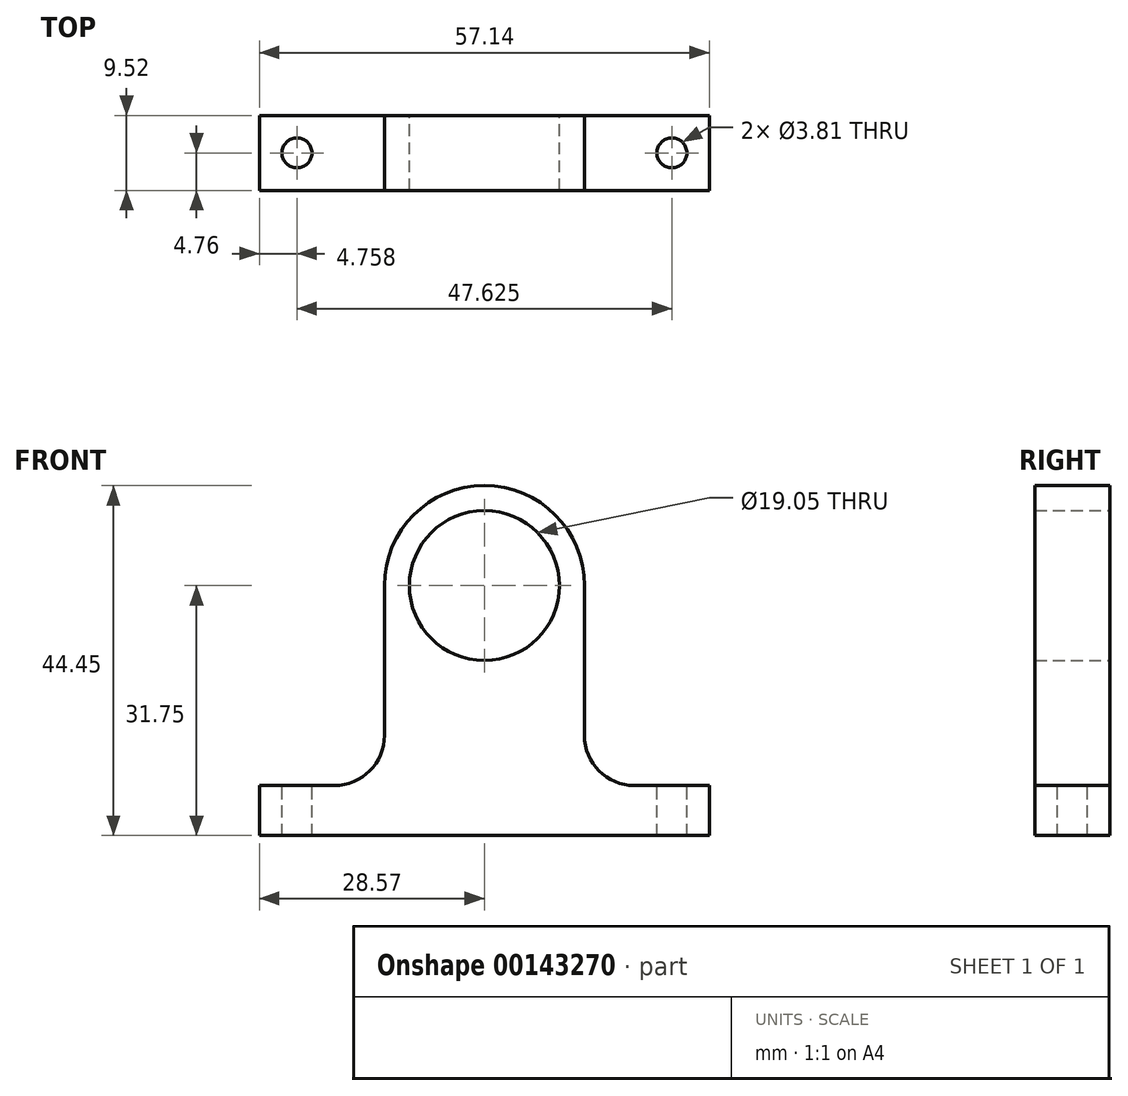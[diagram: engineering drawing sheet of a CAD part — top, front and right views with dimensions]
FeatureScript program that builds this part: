
annotation { "Feature Type Name" : "Feature", "Feature Type Description" : "" }
export const myFeature = defineFeature(function(context is Context, id is Id, definition is map)
    precondition{}
    {
        {
            var Q0;
            Q0=qCreatedBy(makeId("Front.planeOp"),FACE);
            var sketch = newSketch(context, id + "F0", { "sketchPlane" : qUnion([Q0])});
            skCircle(sketch, "E0", {"center": v(0, 0) * mm, "radius": 9.53 * mm});
            skArc(sketch, "E1", {"start": v(12.7, 0) * mm, "mid": v(0, 12.7) * mm, "end": v(-12.7, 0) * mm});
            skLineSegment(sketch, "E2", {"start": v(-12.7, 0) * mm, "end": v(-12.7, -25.4) * mm});
            skLineSegment(sketch, "E3", {"start": v(-12.7, -25.4) * mm, "end": v(-28.57, -25.4) * mm});
            skLineSegment(sketch, "E4", {"start": v(-28.58, -25.4) * mm, "end": v(-28.58, -31.75) * mm});
            skLineSegment(sketch, "E5", {"start": v(-28.58, -31.75) * mm, "end": v(28.57, -31.75) * mm});
            skLineSegment(sketch, "E6", {"start": v(28.57, -31.75) * mm, "end": v(28.57, -25.4) * mm});
            skLineSegment(sketch, "E7", {"start": v(28.57, -25.4) * mm, "end": v(12.7, -25.4) * mm});
            skLineSegment(sketch, "E8", {"start": v(12.7, -25.4) * mm, "end": v(12.7, 0) * mm});
            skCircle(sketch, "E9", {"center": v(0, 0) * mm, "radius": 4.76 * mm});
            skCircle(sketch, "E10", {"center": v(-4.76, 0) * mm, "radius": 4.76 * mm});
            skSolve(sketch);
        }
        {
            var Q0;
            Q0=makeQuery(id+"F0.imprint","IMPRINT",FACE,{"disambiguationData":[TD([[makeQuery(id+"F0.imprint","IMPRINT",EDGE,{"derivedFrom":sQuery(id+"F0.wireOp",EDGE,"E0")}),-1.0]])]});
            extrude(context, id + "F1", {"entities" : qUnion([Q0]), "depth" : 9.52 * mm, "symmetric" : true});
        }
        {
            var Q0;
            Q0=makeQuery(id+"F1.opExtrude","SWEPT_EDGE",EDGE,{"disambiguationData":[OSD([sQuery(id+"F0.wireOp",EDGE,"E2"),sQuery(id+"F0.wireOp",EDGE,"E3")])]});
            var Q1;
            Q1=makeQuery(id+"F1.opExtrude","SWEPT_EDGE",EDGE,{"disambiguationData":[OSD([sQuery(id+"F0.wireOp",EDGE,"E7"),sQuery(id+"F0.wireOp",EDGE,"E8")])]});
            fillet(context, id + "F2", {"entities" : qUnion([Q0, Q1]), "radius" : 6.35 * mm, "tangentPropagation" : true, "allowEdgeOverflow" : false});
        }
        {
            var Q0;
            Q0=makeQuery(id+"F1.opExtrude","SWEPT_FACE",FACE,{"disambiguationData":[OSD([sQuery(id+"F0.wireOp",EDGE,"E5")])]});
            var sketch = newSketch(context, id + "F3", { "sketchPlane" : qUnion([Q0])});
            skCircle(sketch, "E11", {"center": v(-23.81, 0) * mm, "radius": 1.87 * mm});
            skCircle(sketch, "E12", {"center": v(23.81, 0) * mm, "radius": 1.83 * mm});
            skSolve(sketch);
        }
        {
            var Q0;
            Q0=sQuery(id+"F3.wireOp",VERTEX,"E11.center");
            var Q1;
            Q1=sQuery(id+"F3.wireOp",VERTEX,"E12.center");
            var Q2;
            Q2=makeQuery(id+"F1.opExtrude","SWEPT_BODY",BODY,{"disambiguationData":[OSD([sQuery(id+"F0.wireOp",EDGE,"E0"),sQuery(id+"F0.wireOp",EDGE,"E1"),sQuery(id+"F0.wireOp",EDGE,"E2"),sQuery(id+"F0.wireOp",EDGE,"E3"),sQuery(id+"F0.wireOp",EDGE,"E4"),sQuery(id+"F0.wireOp",EDGE,"E5"),sQuery(id+"F0.wireOp",EDGE,"E6"),sQuery(id+"F0.wireOp",EDGE,"E7"),sQuery(id+"F0.wireOp",EDGE,"E8")])]});
            hole(context, id + "F4", {"style" : HoleStyle.SIMPLE, "endStyle" : HoleEndStyle.THROUGH, "holeDiameter" : 3.8 * mm, "locations" : qUnion([Q0, Q1]), "scope" : qUnion([Q2]), "tappedDepth" : 12.7 * mm, "tapClearance" : 3, "startStyle" : HoleStartStyle.PART});
        }
    });
